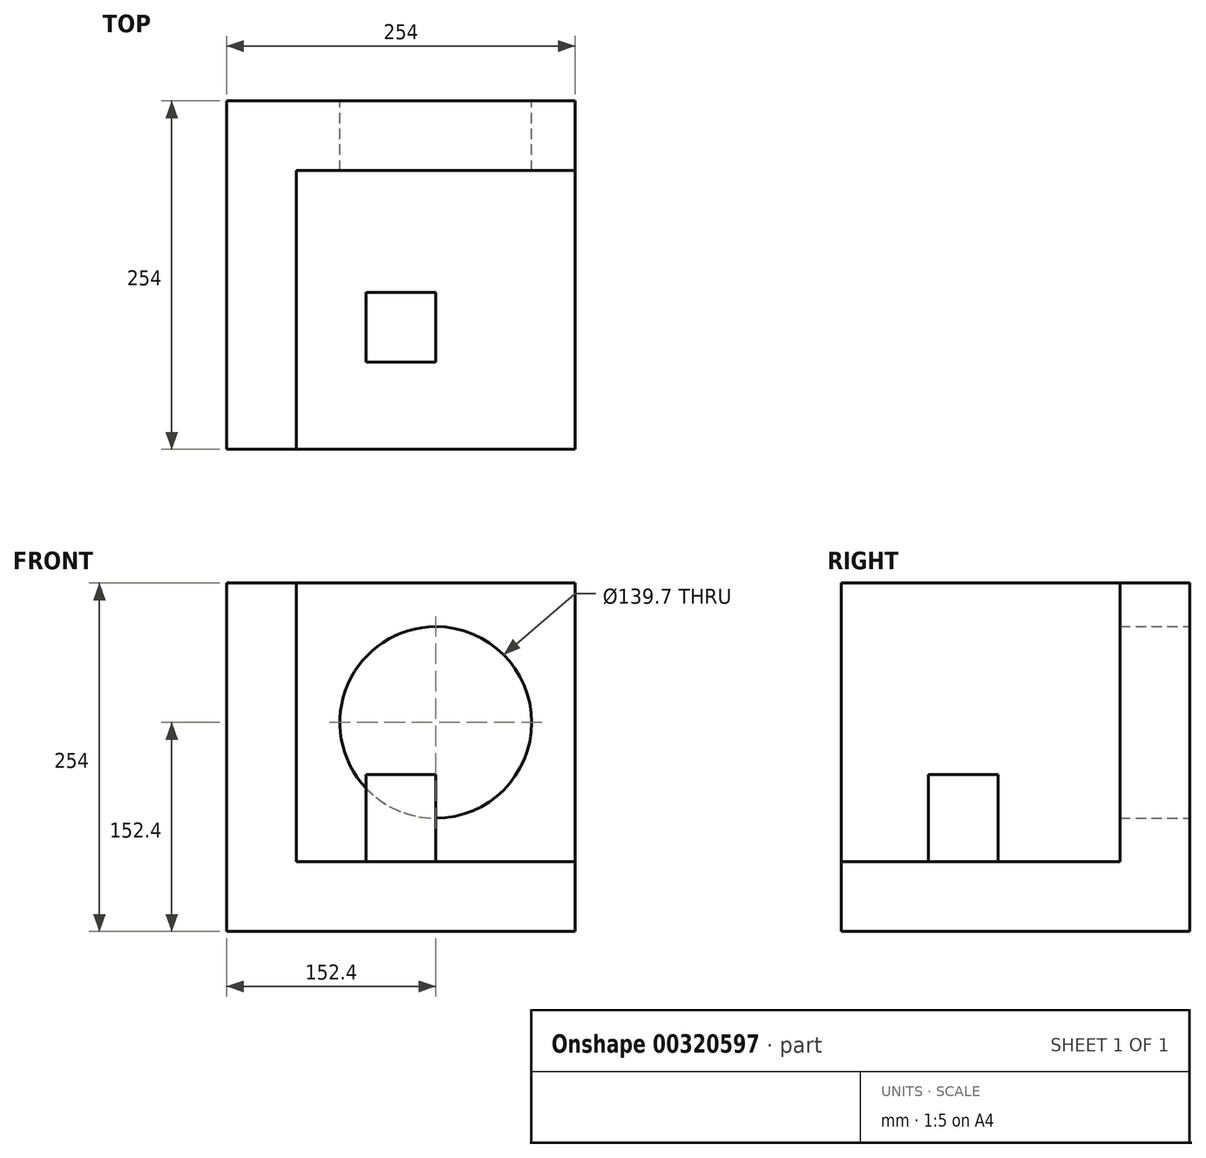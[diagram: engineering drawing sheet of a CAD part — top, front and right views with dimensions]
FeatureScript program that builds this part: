
annotation { "Feature Type Name" : "Feature", "Feature Type Description" : "" }
export const myFeature = defineFeature(function(context is Context, id is Id, definition is map)
    precondition{}
    {
        {
            var Q0;
            Q0=qCreatedBy(makeId("Top.planeOp"),FACE);
            var sketch = newSketch(context, id + "F0", { "sketchPlane" : qUnion([Q0])});
            skLineSegment(sketch, "E0.bottom", {"start": v(0, 0) * mm, "end": v(254, 0) * mm});
            skLineSegment(sketch, "E0.top", {"start": v(0, -254) * mm, "end": v(254, -254) * mm});
            skLineSegment(sketch, "E0.left", {"start": v(0, 0) * mm, "end": v(0, -254) * mm});
            skLineSegment(sketch, "E0.right", {"start": v(254, 0) * mm, "end": v(254, -254) * mm});
            skSolve(sketch);
        }
        {
            var Q0;
            Q0=makeQuery(id+"F0.imprint","IMPRINT",FACE,{"disambiguationData":[TD([[makeQuery(id+"F0.imprint","IMPRINT",EDGE,{"derivedFrom":sQuery(id+"F0.wireOp",EDGE,"E0.bottom")}),-1.0]])]});
            extrude(context, id + "F1", {"entities" : qUnion([Q0]), "depth" : 254 * mm});
        }
        {
            var Q0;
            Q0=qCreatedBy(makeId("Right.planeOp"),FACE);
            cPlane(context, id + "F2", {"entities" : qUnion([Q0]), "cplaneType" : CPlaneType.OFFSET, "offset" : 254 * mm, "width" : 152.4 * mm, "height" : 152.4 * mm});
        }
        {
            var Q0;
            Q0=qCreatedBy(makeId("Right.planeOp"),FACE);
            cPlane(context, id + "F3", {"entities" : qUnion([Q0]), "cplaneType" : CPlaneType.OFFSET, "offset" : 127 * mm, "oppositeDirection" : true, "width" : 152.4 * mm, "height" : 152.4 * mm});
        }
        {
            var Q0;
            Q0=makeQuery(id+"F1.opExtrude","SWEPT_FACE",FACE,{"disambiguationData":[OSD([sQuery(id+"F0.wireOp",EDGE,"E0.top")])]});
            var Q1;
            Q1=makeQuery(id+"F1.opExtrude","SWEPT_FACE",FACE,{"disambiguationData":[OSD([sQuery(id+"F0.wireOp",EDGE,"E0.right")])]});
            var Q2;
            Q2=makeQuery(id+"F1.opExtrude","CAP_FACE",FACE,{"disambiguationData":[OSD([sQuery(id+"F0.wireOp",EDGE,"E0.bottom"),sQuery(id+"F0.wireOp",EDGE,"E0.top"),sQuery(id+"F0.wireOp",EDGE,"E0.left"),sQuery(id+"F0.wireOp",EDGE,"E0.right")])],"isStart":false});
            shell(context, id + "F4", {"entities" : qUnion([Q0, Q1, Q2]), "thickness" : 50.8 * mm});
        }
        {
            var Q0;
            Q0=qCreatedBy(makeId("Front.planeOp"),FACE);
            var sketch = newSketch(context, id + "F5", { "sketchPlane" : qUnion([Q0])});
            skCircle(sketch, "E1", {"center": v(152.4, 152.4) * mm, "radius": 69.85 * mm});
            skSolve(sketch);
        }
        {
            var Q0;
            Q0 = qSketchRegion(id + "F5", true);
            extrude(context, id + "F6", {"entities" : qUnion([Q0]), "operationType" : NewBodyOperationType.REMOVE, "endBound" : BoundingType.THROUGH_ALL, "depth" : 25.4 * mm});
        }
        {
            var Q0;
            Q0=qCreatedBy(makeId("Top.planeOp"),FACE);
            var sketch = newSketch(context, id + "F7", { "sketchPlane" : qUnion([Q0])});
            skLineSegment(sketch, "E2.bottom", {"start": v(101.6, -139.7) * mm, "end": v(152.4, -139.7) * mm});
            skLineSegment(sketch, "E2.top", {"start": v(101.6, -190.5) * mm, "end": v(152.4, -190.5) * mm});
            skLineSegment(sketch, "E2.left", {"start": v(101.6, -139.7) * mm, "end": v(101.6, -190.5) * mm});
            skLineSegment(sketch, "E2.right", {"start": v(152.4, -139.7) * mm, "end": v(152.4, -190.5) * mm});
            skSolve(sketch);
        }
        {
            var Q0;
            Q0 = qSketchRegion(id + "F7", true);
            extrude(context, id + "F8", {"entities" : qUnion([Q0]), "operationType" : NewBodyOperationType.ADD, "depth" : 114.3 * mm});
        }
    });
